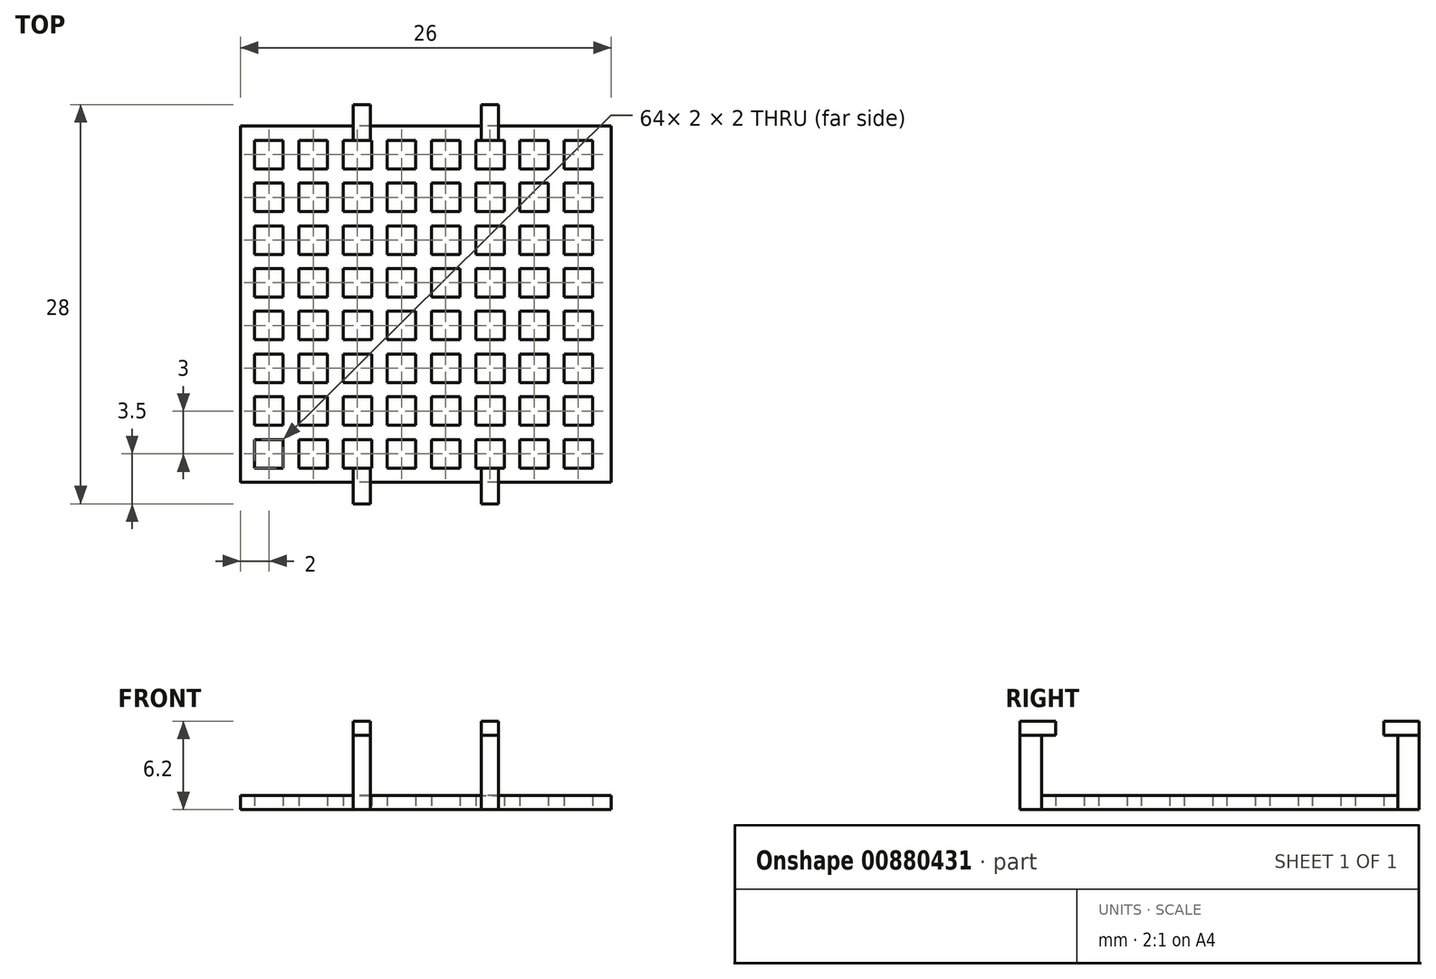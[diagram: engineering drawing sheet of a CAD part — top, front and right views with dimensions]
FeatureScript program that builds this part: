
annotation { "Feature Type Name" : "Feature", "Feature Type Description" : "" }
export const myFeature = defineFeature(function(context is Context, id is Id, definition is map)
    precondition{}
    {
        {
            var Q0;
            Q0=qCreatedBy(makeId("Top.planeOp"),FACE);
            var sketch = newSketch(context, id + "F0", { "sketchPlane" : qUnion([Q0])});
            skLineSegment(sketch, "E0.bottom", {"start": v(13, -12.5) * mm, "end": v(-13, -12.5) * mm});
            skLineSegment(sketch, "E0.top", {"start": v(13, 12.5) * mm, "end": v(-13, 12.5) * mm});
            skLineSegment(sketch, "E0.left", {"start": v(13, -12.5) * mm, "end": v(13, 12.5) * mm});
            skLineSegment(sketch, "E0.right", {"start": v(-13, -12.5) * mm, "end": v(-13, 12.5) * mm});
            skPoint(sketch, "E0.middle", {"position": v(0, 0) * mm});
            skLineSegment(sketch, "E1.bottom", {"start": v(-12, 11.5) * mm, "end": v(-10, 11.5) * mm});
            skLineSegment(sketch, "E1.top", {"start": v(-12, 9.5) * mm, "end": v(-10, 9.5) * mm});
            skLineSegment(sketch, "E1.left", {"start": v(-12, 11.5) * mm, "end": v(-12, 9.5) * mm});
            skLineSegment(sketch, "E1.right", {"start": v(-10, 11.5) * mm, "end": v(-10, 9.5) * mm});
            skLineSegment(sketch, "E2.0.1.0", {"start": v(-12, 8.5) * mm, "end": v(-10, 8.5) * mm});
            skLineSegment(sketch, "E2.0.1.1", {"start": v(-10, 8.5) * mm, "end": v(-10, 6.5) * mm});
            skLineSegment(sketch, "E2.0.1.2", {"start": v(-12, 8.5) * mm, "end": v(-12, 6.5) * mm});
            skLineSegment(sketch, "E2.0.1.3", {"start": v(-12, 6.5) * mm, "end": v(-10, 6.5) * mm});
            skLineSegment(sketch, "E2.0.2.0", {"start": v(-12, 5.5) * mm, "end": v(-10, 5.5) * mm});
            skLineSegment(sketch, "E2.0.2.1", {"start": v(-10, 5.5) * mm, "end": v(-10, 3.5) * mm});
            skLineSegment(sketch, "E2.0.2.2", {"start": v(-12, 5.5) * mm, "end": v(-12, 3.5) * mm});
            skLineSegment(sketch, "E2.0.2.3", {"start": v(-12, 3.5) * mm, "end": v(-10, 3.5) * mm});
            skLineSegment(sketch, "E2.0.3.0", {"start": v(-12, 2.5) * mm, "end": v(-10, 2.5) * mm});
            skLineSegment(sketch, "E2.0.3.1", {"start": v(-10, 2.5) * mm, "end": v(-10, 0.5) * mm});
            skLineSegment(sketch, "E2.0.3.2", {"start": v(-12, 2.5) * mm, "end": v(-12, 0.5) * mm});
            skLineSegment(sketch, "E2.0.3.3", {"start": v(-12, 0.5) * mm, "end": v(-10, 0.5) * mm});
            skLineSegment(sketch, "E2.0.4.0", {"start": v(-12, -0.5) * mm, "end": v(-10, -0.5) * mm});
            skLineSegment(sketch, "E2.0.4.1", {"start": v(-10, -0.5) * mm, "end": v(-10, -2.5) * mm});
            skLineSegment(sketch, "E2.0.4.2", {"start": v(-12, -0.5) * mm, "end": v(-12, -2.5) * mm});
            skLineSegment(sketch, "E2.0.4.3", {"start": v(-12, -2.5) * mm, "end": v(-10, -2.5) * mm});
            skLineSegment(sketch, "E2.0.5.0", {"start": v(-12, -3.5) * mm, "end": v(-10, -3.5) * mm});
            skLineSegment(sketch, "E2.0.5.1", {"start": v(-10, -3.5) * mm, "end": v(-10, -5.5) * mm});
            skLineSegment(sketch, "E2.0.5.2", {"start": v(-12, -3.5) * mm, "end": v(-12, -5.5) * mm});
            skLineSegment(sketch, "E2.0.5.3", {"start": v(-12, -5.5) * mm, "end": v(-10, -5.5) * mm});
            skLineSegment(sketch, "E2.0.6.0", {"start": v(-12, -6.5) * mm, "end": v(-10, -6.5) * mm});
            skLineSegment(sketch, "E2.0.6.1", {"start": v(-10, -6.5) * mm, "end": v(-10, -8.5) * mm});
            skLineSegment(sketch, "E2.0.6.2", {"start": v(-12, -6.5) * mm, "end": v(-12, -8.5) * mm});
            skLineSegment(sketch, "E2.0.6.3", {"start": v(-12, -8.5) * mm, "end": v(-10, -8.5) * mm});
            skLineSegment(sketch, "E2.0.7.0", {"start": v(-12, -9.5) * mm, "end": v(-10, -9.5) * mm});
            skLineSegment(sketch, "E2.0.7.1", {"start": v(-10, -9.5) * mm, "end": v(-10, -11.5) * mm});
            skLineSegment(sketch, "E2.0.7.2", {"start": v(-12, -9.5) * mm, "end": v(-12, -11.5) * mm});
            skLineSegment(sketch, "E2.0.7.3", {"start": v(-12, -11.5) * mm, "end": v(-10, -11.5) * mm});
            skLineSegment(sketch, "E2.1.0.0", {"start": v(-8.9, 11.5) * mm, "end": v(-6.9, 11.5) * mm});
            skLineSegment(sketch, "E2.1.0.1", {"start": v(-6.9, 11.5) * mm, "end": v(-6.9, 9.5) * mm});
            skLineSegment(sketch, "E2.1.0.2", {"start": v(-8.9, 11.5) * mm, "end": v(-8.9, 9.5) * mm});
            skLineSegment(sketch, "E2.1.0.3", {"start": v(-8.9, 9.5) * mm, "end": v(-6.9, 9.5) * mm});
            skLineSegment(sketch, "E2.1.1.0", {"start": v(-8.9, 8.5) * mm, "end": v(-6.9, 8.5) * mm});
            skLineSegment(sketch, "E2.1.1.1", {"start": v(-6.9, 8.5) * mm, "end": v(-6.9, 6.5) * mm});
            skLineSegment(sketch, "E2.1.1.2", {"start": v(-8.9, 8.5) * mm, "end": v(-8.9, 6.5) * mm});
            skLineSegment(sketch, "E2.1.1.3", {"start": v(-8.9, 6.5) * mm, "end": v(-6.9, 6.5) * mm});
            skLineSegment(sketch, "E2.1.2.0", {"start": v(-8.9, 5.5) * mm, "end": v(-6.9, 5.5) * mm});
            skLineSegment(sketch, "E2.1.2.1", {"start": v(-6.9, 5.5) * mm, "end": v(-6.9, 3.5) * mm});
            skLineSegment(sketch, "E2.1.2.2", {"start": v(-8.9, 5.5) * mm, "end": v(-8.9, 3.5) * mm});
            skLineSegment(sketch, "E2.1.2.3", {"start": v(-8.9, 3.5) * mm, "end": v(-6.9, 3.5) * mm});
            skLineSegment(sketch, "E2.1.3.0", {"start": v(-8.9, 2.5) * mm, "end": v(-6.9, 2.5) * mm});
            skLineSegment(sketch, "E2.1.3.1", {"start": v(-6.9, 2.5) * mm, "end": v(-6.9, 0.5) * mm});
            skLineSegment(sketch, "E2.1.3.2", {"start": v(-8.9, 2.5) * mm, "end": v(-8.9, 0.5) * mm});
            skLineSegment(sketch, "E2.1.3.3", {"start": v(-8.9, 0.5) * mm, "end": v(-6.9, 0.5) * mm});
            skLineSegment(sketch, "E2.1.4.0", {"start": v(-8.9, -0.5) * mm, "end": v(-6.9, -0.5) * mm});
            skLineSegment(sketch, "E2.1.4.1", {"start": v(-6.9, -0.5) * mm, "end": v(-6.9, -2.5) * mm});
            skLineSegment(sketch, "E2.1.4.2", {"start": v(-8.9, -0.5) * mm, "end": v(-8.9, -2.5) * mm});
            skLineSegment(sketch, "E2.1.4.3", {"start": v(-8.9, -2.5) * mm, "end": v(-6.9, -2.5) * mm});
            skLineSegment(sketch, "E2.1.5.0", {"start": v(-8.9, -3.5) * mm, "end": v(-6.9, -3.5) * mm});
            skLineSegment(sketch, "E2.1.5.1", {"start": v(-6.9, -3.5) * mm, "end": v(-6.9, -5.5) * mm});
            skLineSegment(sketch, "E2.1.5.2", {"start": v(-8.9, -3.5) * mm, "end": v(-8.9, -5.5) * mm});
            skLineSegment(sketch, "E2.1.5.3", {"start": v(-8.9, -5.5) * mm, "end": v(-6.9, -5.5) * mm});
            skLineSegment(sketch, "E2.1.6.0", {"start": v(-8.9, -6.5) * mm, "end": v(-6.9, -6.5) * mm});
            skLineSegment(sketch, "E2.1.6.1", {"start": v(-6.9, -6.5) * mm, "end": v(-6.9, -8.5) * mm});
            skLineSegment(sketch, "E2.1.6.2", {"start": v(-8.9, -6.5) * mm, "end": v(-8.9, -8.5) * mm});
            skLineSegment(sketch, "E2.1.6.3", {"start": v(-8.9, -8.5) * mm, "end": v(-6.9, -8.5) * mm});
            skLineSegment(sketch, "E2.1.7.0", {"start": v(-8.9, -9.5) * mm, "end": v(-6.9, -9.5) * mm});
            skLineSegment(sketch, "E2.1.7.1", {"start": v(-6.9, -9.5) * mm, "end": v(-6.9, -11.5) * mm});
            skLineSegment(sketch, "E2.1.7.2", {"start": v(-8.9, -9.5) * mm, "end": v(-8.9, -11.5) * mm});
            skLineSegment(sketch, "E2.1.7.3", {"start": v(-8.9, -11.5) * mm, "end": v(-6.9, -11.5) * mm});
            skLineSegment(sketch, "E2.2.0.0", {"start": v(-5.8, 11.5) * mm, "end": v(-3.8, 11.5) * mm});
            skLineSegment(sketch, "E2.2.0.1", {"start": v(-3.8, 11.5) * mm, "end": v(-3.8, 9.5) * mm});
            skLineSegment(sketch, "E2.2.0.2", {"start": v(-5.8, 11.5) * mm, "end": v(-5.8, 9.5) * mm});
            skLineSegment(sketch, "E2.2.0.3", {"start": v(-5.8, 9.5) * mm, "end": v(-3.8, 9.5) * mm});
            skLineSegment(sketch, "E2.2.1.0", {"start": v(-5.8, 8.5) * mm, "end": v(-3.8, 8.5) * mm});
            skLineSegment(sketch, "E2.2.1.1", {"start": v(-3.8, 8.5) * mm, "end": v(-3.8, 6.5) * mm});
            skLineSegment(sketch, "E2.2.1.2", {"start": v(-5.8, 8.5) * mm, "end": v(-5.8, 6.5) * mm});
            skLineSegment(sketch, "E2.2.1.3", {"start": v(-5.8, 6.5) * mm, "end": v(-3.8, 6.5) * mm});
            skLineSegment(sketch, "E2.2.2.0", {"start": v(-5.8, 5.5) * mm, "end": v(-3.8, 5.5) * mm});
            skLineSegment(sketch, "E2.2.2.1", {"start": v(-3.8, 5.5) * mm, "end": v(-3.8, 3.5) * mm});
            skLineSegment(sketch, "E2.2.2.2", {"start": v(-5.8, 5.5) * mm, "end": v(-5.8, 3.5) * mm});
            skLineSegment(sketch, "E2.2.2.3", {"start": v(-5.8, 3.5) * mm, "end": v(-3.8, 3.5) * mm});
            skLineSegment(sketch, "E2.2.3.0", {"start": v(-5.8, 2.5) * mm, "end": v(-3.8, 2.5) * mm});
            skLineSegment(sketch, "E2.2.3.1", {"start": v(-3.8, 2.5) * mm, "end": v(-3.8, 0.5) * mm});
            skLineSegment(sketch, "E2.2.3.2", {"start": v(-5.8, 2.5) * mm, "end": v(-5.8, 0.5) * mm});
            skLineSegment(sketch, "E2.2.3.3", {"start": v(-5.8, 0.5) * mm, "end": v(-3.8, 0.5) * mm});
            skLineSegment(sketch, "E2.2.4.0", {"start": v(-5.8, -0.5) * mm, "end": v(-3.8, -0.5) * mm});
            skLineSegment(sketch, "E2.2.4.1", {"start": v(-3.8, -0.5) * mm, "end": v(-3.8, -2.5) * mm});
            skLineSegment(sketch, "E2.2.4.2", {"start": v(-5.8, -0.5) * mm, "end": v(-5.8, -2.5) * mm});
            skLineSegment(sketch, "E2.2.4.3", {"start": v(-5.8, -2.5) * mm, "end": v(-3.8, -2.5) * mm});
            skLineSegment(sketch, "E2.2.5.0", {"start": v(-5.8, -3.5) * mm, "end": v(-3.8, -3.5) * mm});
            skLineSegment(sketch, "E2.2.5.1", {"start": v(-3.8, -3.5) * mm, "end": v(-3.8, -5.5) * mm});
            skLineSegment(sketch, "E2.2.5.2", {"start": v(-5.8, -3.5) * mm, "end": v(-5.8, -5.5) * mm});
            skLineSegment(sketch, "E2.2.5.3", {"start": v(-5.8, -5.5) * mm, "end": v(-3.8, -5.5) * mm});
            skLineSegment(sketch, "E2.2.6.0", {"start": v(-5.8, -6.5) * mm, "end": v(-3.8, -6.5) * mm});
            skLineSegment(sketch, "E2.2.6.1", {"start": v(-3.8, -6.5) * mm, "end": v(-3.8, -8.5) * mm});
            skLineSegment(sketch, "E2.2.6.2", {"start": v(-5.8, -6.5) * mm, "end": v(-5.8, -8.5) * mm});
            skLineSegment(sketch, "E2.2.6.3", {"start": v(-5.8, -8.5) * mm, "end": v(-3.8, -8.5) * mm});
            skLineSegment(sketch, "E2.2.7.0", {"start": v(-5.8, -9.5) * mm, "end": v(-3.8, -9.5) * mm});
            skLineSegment(sketch, "E2.2.7.1", {"start": v(-3.8, -9.5) * mm, "end": v(-3.8, -11.5) * mm});
            skLineSegment(sketch, "E2.2.7.2", {"start": v(-5.8, -9.5) * mm, "end": v(-5.8, -11.5) * mm});
            skLineSegment(sketch, "E2.2.7.3", {"start": v(-5.8, -11.5) * mm, "end": v(-3.8, -11.5) * mm});
            skLineSegment(sketch, "E2.3.0.0", {"start": v(-2.7, 11.5) * mm, "end": v(-0.7, 11.5) * mm});
            skLineSegment(sketch, "E2.3.0.1", {"start": v(-0.7, 11.5) * mm, "end": v(-0.7, 9.5) * mm});
            skLineSegment(sketch, "E2.3.0.2", {"start": v(-2.7, 11.5) * mm, "end": v(-2.7, 9.5) * mm});
            skLineSegment(sketch, "E2.3.0.3", {"start": v(-2.7, 9.5) * mm, "end": v(-0.7, 9.5) * mm});
            skLineSegment(sketch, "E2.3.1.0", {"start": v(-2.7, 8.5) * mm, "end": v(-0.7, 8.5) * mm});
            skLineSegment(sketch, "E2.3.1.1", {"start": v(-0.7, 8.5) * mm, "end": v(-0.7, 6.5) * mm});
            skLineSegment(sketch, "E2.3.1.2", {"start": v(-2.7, 8.5) * mm, "end": v(-2.7, 6.5) * mm});
            skLineSegment(sketch, "E2.3.1.3", {"start": v(-2.7, 6.5) * mm, "end": v(-0.7, 6.5) * mm});
            skLineSegment(sketch, "E2.3.2.0", {"start": v(-2.7, 5.5) * mm, "end": v(-0.7, 5.5) * mm});
            skLineSegment(sketch, "E2.3.2.1", {"start": v(-0.7, 5.5) * mm, "end": v(-0.7, 3.5) * mm});
            skLineSegment(sketch, "E2.3.2.2", {"start": v(-2.7, 5.5) * mm, "end": v(-2.7, 3.5) * mm});
            skLineSegment(sketch, "E2.3.2.3", {"start": v(-2.7, 3.5) * mm, "end": v(-0.7, 3.5) * mm});
            skLineSegment(sketch, "E2.3.3.0", {"start": v(-2.7, 2.5) * mm, "end": v(-0.7, 2.5) * mm});
            skLineSegment(sketch, "E2.3.3.1", {"start": v(-0.7, 2.5) * mm, "end": v(-0.7, 0.5) * mm});
            skLineSegment(sketch, "E2.3.3.2", {"start": v(-2.7, 2.5) * mm, "end": v(-2.7, 0.5) * mm});
            skLineSegment(sketch, "E2.3.3.3", {"start": v(-2.7, 0.5) * mm, "end": v(-0.7, 0.5) * mm});
            skLineSegment(sketch, "E2.3.4.0", {"start": v(-2.7, -0.5) * mm, "end": v(-0.7, -0.5) * mm});
            skLineSegment(sketch, "E2.3.4.1", {"start": v(-0.7, -0.5) * mm, "end": v(-0.7, -2.5) * mm});
            skLineSegment(sketch, "E2.3.4.2", {"start": v(-2.7, -0.5) * mm, "end": v(-2.7, -2.5) * mm});
            skLineSegment(sketch, "E2.3.4.3", {"start": v(-2.7, -2.5) * mm, "end": v(-0.7, -2.5) * mm});
            skLineSegment(sketch, "E2.3.5.0", {"start": v(-2.7, -3.5) * mm, "end": v(-0.7, -3.5) * mm});
            skLineSegment(sketch, "E2.3.5.1", {"start": v(-0.7, -3.5) * mm, "end": v(-0.7, -5.5) * mm});
            skLineSegment(sketch, "E2.3.5.2", {"start": v(-2.7, -3.5) * mm, "end": v(-2.7, -5.5) * mm});
            skLineSegment(sketch, "E2.3.5.3", {"start": v(-2.7, -5.5) * mm, "end": v(-0.7, -5.5) * mm});
            skLineSegment(sketch, "E2.3.6.0", {"start": v(-2.7, -6.5) * mm, "end": v(-0.7, -6.5) * mm});
            skLineSegment(sketch, "E2.3.6.1", {"start": v(-0.7, -6.5) * mm, "end": v(-0.7, -8.5) * mm});
            skLineSegment(sketch, "E2.3.6.2", {"start": v(-2.7, -6.5) * mm, "end": v(-2.7, -8.5) * mm});
            skLineSegment(sketch, "E2.3.6.3", {"start": v(-2.7, -8.5) * mm, "end": v(-0.7, -8.5) * mm});
            skLineSegment(sketch, "E2.3.7.0", {"start": v(-2.7, -9.5) * mm, "end": v(-0.7, -9.5) * mm});
            skLineSegment(sketch, "E2.3.7.1", {"start": v(-0.7, -9.5) * mm, "end": v(-0.7, -11.5) * mm});
            skLineSegment(sketch, "E2.3.7.2", {"start": v(-2.7, -9.5) * mm, "end": v(-2.7, -11.5) * mm});
            skLineSegment(sketch, "E2.3.7.3", {"start": v(-2.7, -11.5) * mm, "end": v(-0.7, -11.5) * mm});
            skLineSegment(sketch, "E2.4.0.0", {"start": v(0.4, 11.5) * mm, "end": v(2.4, 11.5) * mm});
            skLineSegment(sketch, "E2.4.0.1", {"start": v(2.4, 11.5) * mm, "end": v(2.4, 9.5) * mm});
            skLineSegment(sketch, "E2.4.0.2", {"start": v(0.4, 11.5) * mm, "end": v(0.4, 9.5) * mm});
            skLineSegment(sketch, "E2.4.0.3", {"start": v(0.4, 9.5) * mm, "end": v(2.4, 9.5) * mm});
            skLineSegment(sketch, "E2.4.1.0", {"start": v(0.4, 8.5) * mm, "end": v(2.4, 8.5) * mm});
            skLineSegment(sketch, "E2.4.1.1", {"start": v(2.4, 8.5) * mm, "end": v(2.4, 6.5) * mm});
            skLineSegment(sketch, "E2.4.1.2", {"start": v(0.4, 8.5) * mm, "end": v(0.4, 6.5) * mm});
            skLineSegment(sketch, "E2.4.1.3", {"start": v(0.4, 6.5) * mm, "end": v(2.4, 6.5) * mm});
            skLineSegment(sketch, "E2.4.2.0", {"start": v(0.4, 5.5) * mm, "end": v(2.4, 5.5) * mm});
            skLineSegment(sketch, "E2.4.2.1", {"start": v(2.4, 5.5) * mm, "end": v(2.4, 3.5) * mm});
            skLineSegment(sketch, "E2.4.2.2", {"start": v(0.4, 5.5) * mm, "end": v(0.4, 3.5) * mm});
            skLineSegment(sketch, "E2.4.2.3", {"start": v(0.4, 3.5) * mm, "end": v(2.4, 3.5) * mm});
            skLineSegment(sketch, "E2.4.3.0", {"start": v(0.4, 2.5) * mm, "end": v(2.4, 2.5) * mm});
            skLineSegment(sketch, "E2.4.3.1", {"start": v(2.4, 2.5) * mm, "end": v(2.4, 0.5) * mm});
            skLineSegment(sketch, "E2.4.3.2", {"start": v(0.4, 2.5) * mm, "end": v(0.4, 0.5) * mm});
            skLineSegment(sketch, "E2.4.3.3", {"start": v(0.4, 0.5) * mm, "end": v(2.4, 0.5) * mm});
            skLineSegment(sketch, "E2.4.4.0", {"start": v(0.4, -0.5) * mm, "end": v(2.4, -0.5) * mm});
            skLineSegment(sketch, "E2.4.4.1", {"start": v(2.4, -0.5) * mm, "end": v(2.4, -2.5) * mm});
            skLineSegment(sketch, "E2.4.4.2", {"start": v(0.4, -0.5) * mm, "end": v(0.4, -2.5) * mm});
            skLineSegment(sketch, "E2.4.4.3", {"start": v(0.4, -2.5) * mm, "end": v(2.4, -2.5) * mm});
            skLineSegment(sketch, "E2.4.5.0", {"start": v(0.4, -3.5) * mm, "end": v(2.4, -3.5) * mm});
            skLineSegment(sketch, "E2.4.5.1", {"start": v(2.4, -3.5) * mm, "end": v(2.4, -5.5) * mm});
            skLineSegment(sketch, "E2.4.5.2", {"start": v(0.4, -3.5) * mm, "end": v(0.4, -5.5) * mm});
            skLineSegment(sketch, "E2.4.5.3", {"start": v(0.4, -5.5) * mm, "end": v(2.4, -5.5) * mm});
            skLineSegment(sketch, "E2.4.6.0", {"start": v(0.4, -6.5) * mm, "end": v(2.4, -6.5) * mm});
            skLineSegment(sketch, "E2.4.6.1", {"start": v(2.4, -6.5) * mm, "end": v(2.4, -8.5) * mm});
            skLineSegment(sketch, "E2.4.6.2", {"start": v(0.4, -6.5) * mm, "end": v(0.4, -8.5) * mm});
            skLineSegment(sketch, "E2.4.6.3", {"start": v(0.4, -8.5) * mm, "end": v(2.4, -8.5) * mm});
            skLineSegment(sketch, "E2.4.7.0", {"start": v(0.4, -9.5) * mm, "end": v(2.4, -9.5) * mm});
            skLineSegment(sketch, "E2.4.7.1", {"start": v(2.4, -9.5) * mm, "end": v(2.4, -11.5) * mm});
            skLineSegment(sketch, "E2.4.7.2", {"start": v(0.4, -9.5) * mm, "end": v(0.4, -11.5) * mm});
            skLineSegment(sketch, "E2.4.7.3", {"start": v(0.4, -11.5) * mm, "end": v(2.4, -11.5) * mm});
            skLineSegment(sketch, "E2.5.0.0", {"start": v(3.5, 11.5) * mm, "end": v(5.5, 11.5) * mm});
            skLineSegment(sketch, "E2.5.0.1", {"start": v(5.5, 11.5) * mm, "end": v(5.5, 9.5) * mm});
            skLineSegment(sketch, "E2.5.0.2", {"start": v(3.5, 11.5) * mm, "end": v(3.5, 9.5) * mm});
            skLineSegment(sketch, "E2.5.0.3", {"start": v(3.5, 9.5) * mm, "end": v(5.5, 9.5) * mm});
            skLineSegment(sketch, "E2.5.1.0", {"start": v(3.5, 8.5) * mm, "end": v(5.5, 8.5) * mm});
            skLineSegment(sketch, "E2.5.1.1", {"start": v(5.5, 8.5) * mm, "end": v(5.5, 6.5) * mm});
            skLineSegment(sketch, "E2.5.1.2", {"start": v(3.5, 8.5) * mm, "end": v(3.5, 6.5) * mm});
            skLineSegment(sketch, "E2.5.1.3", {"start": v(3.5, 6.5) * mm, "end": v(5.5, 6.5) * mm});
            skLineSegment(sketch, "E2.5.2.0", {"start": v(3.5, 5.5) * mm, "end": v(5.5, 5.5) * mm});
            skLineSegment(sketch, "E2.5.2.1", {"start": v(5.5, 5.5) * mm, "end": v(5.5, 3.5) * mm});
            skLineSegment(sketch, "E2.5.2.2", {"start": v(3.5, 5.5) * mm, "end": v(3.5, 3.5) * mm});
            skLineSegment(sketch, "E2.5.2.3", {"start": v(3.5, 3.5) * mm, "end": v(5.5, 3.5) * mm});
            skLineSegment(sketch, "E2.5.3.0", {"start": v(3.5, 2.5) * mm, "end": v(5.5, 2.5) * mm});
            skLineSegment(sketch, "E2.5.3.1", {"start": v(5.5, 2.5) * mm, "end": v(5.5, 0.5) * mm});
            skLineSegment(sketch, "E2.5.3.2", {"start": v(3.5, 2.5) * mm, "end": v(3.5, 0.5) * mm});
            skLineSegment(sketch, "E2.5.3.3", {"start": v(3.5, 0.5) * mm, "end": v(5.5, 0.5) * mm});
            skLineSegment(sketch, "E2.5.4.0", {"start": v(3.5, -0.5) * mm, "end": v(5.5, -0.5) * mm});
            skLineSegment(sketch, "E2.5.4.1", {"start": v(5.5, -0.5) * mm, "end": v(5.5, -2.5) * mm});
            skLineSegment(sketch, "E2.5.4.2", {"start": v(3.5, -0.5) * mm, "end": v(3.5, -2.5) * mm});
            skLineSegment(sketch, "E2.5.4.3", {"start": v(3.5, -2.5) * mm, "end": v(5.5, -2.5) * mm});
            skLineSegment(sketch, "E2.5.5.0", {"start": v(3.5, -3.5) * mm, "end": v(5.5, -3.5) * mm});
            skLineSegment(sketch, "E2.5.5.1", {"start": v(5.5, -3.5) * mm, "end": v(5.5, -5.5) * mm});
            skLineSegment(sketch, "E2.5.5.2", {"start": v(3.5, -3.5) * mm, "end": v(3.5, -5.5) * mm});
            skLineSegment(sketch, "E2.5.5.3", {"start": v(3.5, -5.5) * mm, "end": v(5.5, -5.5) * mm});
            skLineSegment(sketch, "E2.5.6.0", {"start": v(3.5, -6.5) * mm, "end": v(5.5, -6.5) * mm});
            skLineSegment(sketch, "E2.5.6.1", {"start": v(5.5, -6.5) * mm, "end": v(5.5, -8.5) * mm});
            skLineSegment(sketch, "E2.5.6.2", {"start": v(3.5, -6.5) * mm, "end": v(3.5, -8.5) * mm});
            skLineSegment(sketch, "E2.5.6.3", {"start": v(3.5, -8.5) * mm, "end": v(5.5, -8.5) * mm});
            skLineSegment(sketch, "E2.5.7.0", {"start": v(3.5, -9.5) * mm, "end": v(5.5, -9.5) * mm});
            skLineSegment(sketch, "E2.5.7.1", {"start": v(5.5, -9.5) * mm, "end": v(5.5, -11.5) * mm});
            skLineSegment(sketch, "E2.5.7.2", {"start": v(3.5, -9.5) * mm, "end": v(3.5, -11.5) * mm});
            skLineSegment(sketch, "E2.5.7.3", {"start": v(3.5, -11.5) * mm, "end": v(5.5, -11.5) * mm});
            skLineSegment(sketch, "E2.6.0.0", {"start": v(6.6, 11.5) * mm, "end": v(8.6, 11.5) * mm});
            skLineSegment(sketch, "E2.6.0.1", {"start": v(8.6, 11.5) * mm, "end": v(8.6, 9.5) * mm});
            skLineSegment(sketch, "E2.6.0.2", {"start": v(6.6, 11.5) * mm, "end": v(6.6, 9.5) * mm});
            skLineSegment(sketch, "E2.6.0.3", {"start": v(6.6, 9.5) * mm, "end": v(8.6, 9.5) * mm});
            skLineSegment(sketch, "E2.6.1.0", {"start": v(6.6, 8.5) * mm, "end": v(8.6, 8.5) * mm});
            skLineSegment(sketch, "E2.6.1.1", {"start": v(8.6, 8.5) * mm, "end": v(8.6, 6.5) * mm});
            skLineSegment(sketch, "E2.6.1.2", {"start": v(6.6, 8.5) * mm, "end": v(6.6, 6.5) * mm});
            skLineSegment(sketch, "E2.6.1.3", {"start": v(6.6, 6.5) * mm, "end": v(8.6, 6.5) * mm});
            skLineSegment(sketch, "E2.6.2.0", {"start": v(6.6, 5.5) * mm, "end": v(8.6, 5.5) * mm});
            skLineSegment(sketch, "E2.6.2.1", {"start": v(8.6, 5.5) * mm, "end": v(8.6, 3.5) * mm});
            skLineSegment(sketch, "E2.6.2.2", {"start": v(6.6, 5.5) * mm, "end": v(6.6, 3.5) * mm});
            skLineSegment(sketch, "E2.6.2.3", {"start": v(6.6, 3.5) * mm, "end": v(8.6, 3.5) * mm});
            skLineSegment(sketch, "E2.6.3.0", {"start": v(6.6, 2.5) * mm, "end": v(8.6, 2.5) * mm});
            skLineSegment(sketch, "E2.6.3.1", {"start": v(8.6, 2.5) * mm, "end": v(8.6, 0.5) * mm});
            skLineSegment(sketch, "E2.6.3.2", {"start": v(6.6, 2.5) * mm, "end": v(6.6, 0.5) * mm});
            skLineSegment(sketch, "E2.6.3.3", {"start": v(6.6, 0.5) * mm, "end": v(8.6, 0.5) * mm});
            skLineSegment(sketch, "E2.6.4.0", {"start": v(6.6, -0.5) * mm, "end": v(8.6, -0.5) * mm});
            skLineSegment(sketch, "E2.6.4.1", {"start": v(8.6, -0.5) * mm, "end": v(8.6, -2.5) * mm});
            skLineSegment(sketch, "E2.6.4.2", {"start": v(6.6, -0.5) * mm, "end": v(6.6, -2.5) * mm});
            skLineSegment(sketch, "E2.6.4.3", {"start": v(6.6, -2.5) * mm, "end": v(8.6, -2.5) * mm});
            skLineSegment(sketch, "E2.6.5.0", {"start": v(6.6, -3.5) * mm, "end": v(8.6, -3.5) * mm});
            skLineSegment(sketch, "E2.6.5.1", {"start": v(8.6, -3.5) * mm, "end": v(8.6, -5.5) * mm});
            skLineSegment(sketch, "E2.6.5.2", {"start": v(6.6, -3.5) * mm, "end": v(6.6, -5.5) * mm});
            skLineSegment(sketch, "E2.6.5.3", {"start": v(6.6, -5.5) * mm, "end": v(8.6, -5.5) * mm});
            skLineSegment(sketch, "E2.6.6.0", {"start": v(6.6, -6.5) * mm, "end": v(8.6, -6.5) * mm});
            skLineSegment(sketch, "E2.6.6.1", {"start": v(8.6, -6.5) * mm, "end": v(8.6, -8.5) * mm});
            skLineSegment(sketch, "E2.6.6.2", {"start": v(6.6, -6.5) * mm, "end": v(6.6, -8.5) * mm});
            skLineSegment(sketch, "E2.6.6.3", {"start": v(6.6, -8.5) * mm, "end": v(8.6, -8.5) * mm});
            skLineSegment(sketch, "E2.6.7.0", {"start": v(6.6, -9.5) * mm, "end": v(8.6, -9.5) * mm});
            skLineSegment(sketch, "E2.6.7.1", {"start": v(8.6, -9.5) * mm, "end": v(8.6, -11.5) * mm});
            skLineSegment(sketch, "E2.6.7.2", {"start": v(6.6, -9.5) * mm, "end": v(6.6, -11.5) * mm});
            skLineSegment(sketch, "E2.6.7.3", {"start": v(6.6, -11.5) * mm, "end": v(8.6, -11.5) * mm});
            skLineSegment(sketch, "E2.7.0.0", {"start": v(9.7, 11.5) * mm, "end": v(11.7, 11.5) * mm});
            skLineSegment(sketch, "E2.7.0.1", {"start": v(11.7, 11.5) * mm, "end": v(11.7, 9.5) * mm});
            skLineSegment(sketch, "E2.7.0.2", {"start": v(9.7, 11.5) * mm, "end": v(9.7, 9.5) * mm});
            skLineSegment(sketch, "E2.7.0.3", {"start": v(9.7, 9.5) * mm, "end": v(11.7, 9.5) * mm});
            skLineSegment(sketch, "E2.7.1.0", {"start": v(9.7, 8.5) * mm, "end": v(11.7, 8.5) * mm});
            skLineSegment(sketch, "E2.7.1.1", {"start": v(11.7, 8.5) * mm, "end": v(11.7, 6.5) * mm});
            skLineSegment(sketch, "E2.7.1.2", {"start": v(9.7, 8.5) * mm, "end": v(9.7, 6.5) * mm});
            skLineSegment(sketch, "E2.7.1.3", {"start": v(9.7, 6.5) * mm, "end": v(11.7, 6.5) * mm});
            skLineSegment(sketch, "E2.7.2.0", {"start": v(9.7, 5.5) * mm, "end": v(11.7, 5.5) * mm});
            skLineSegment(sketch, "E2.7.2.1", {"start": v(11.7, 5.5) * mm, "end": v(11.7, 3.5) * mm});
            skLineSegment(sketch, "E2.7.2.2", {"start": v(9.7, 5.5) * mm, "end": v(9.7, 3.5) * mm});
            skLineSegment(sketch, "E2.7.2.3", {"start": v(9.7, 3.5) * mm, "end": v(11.7, 3.5) * mm});
            skLineSegment(sketch, "E2.7.3.0", {"start": v(9.7, 2.5) * mm, "end": v(11.7, 2.5) * mm});
            skLineSegment(sketch, "E2.7.3.1", {"start": v(11.7, 2.5) * mm, "end": v(11.7, 0.5) * mm});
            skLineSegment(sketch, "E2.7.3.2", {"start": v(9.7, 2.5) * mm, "end": v(9.7, 0.5) * mm});
            skLineSegment(sketch, "E2.7.3.3", {"start": v(9.7, 0.5) * mm, "end": v(11.7, 0.5) * mm});
            skLineSegment(sketch, "E2.7.4.0", {"start": v(9.7, -0.5) * mm, "end": v(11.7, -0.5) * mm});
            skLineSegment(sketch, "E2.7.4.1", {"start": v(11.7, -0.5) * mm, "end": v(11.7, -2.5) * mm});
            skLineSegment(sketch, "E2.7.4.2", {"start": v(9.7, -0.5) * mm, "end": v(9.7, -2.5) * mm});
            skLineSegment(sketch, "E2.7.4.3", {"start": v(9.7, -2.5) * mm, "end": v(11.7, -2.5) * mm});
            skLineSegment(sketch, "E2.7.5.0", {"start": v(9.7, -3.5) * mm, "end": v(11.7, -3.5) * mm});
            skLineSegment(sketch, "E2.7.5.1", {"start": v(11.7, -3.5) * mm, "end": v(11.7, -5.5) * mm});
            skLineSegment(sketch, "E2.7.5.2", {"start": v(9.7, -3.5) * mm, "end": v(9.7, -5.5) * mm});
            skLineSegment(sketch, "E2.7.5.3", {"start": v(9.7, -5.5) * mm, "end": v(11.7, -5.5) * mm});
            skLineSegment(sketch, "E2.7.6.0", {"start": v(9.7, -6.5) * mm, "end": v(11.7, -6.5) * mm});
            skLineSegment(sketch, "E2.7.6.1", {"start": v(11.7, -6.5) * mm, "end": v(11.7, -8.5) * mm});
            skLineSegment(sketch, "E2.7.6.2", {"start": v(9.7, -6.5) * mm, "end": v(9.7, -8.5) * mm});
            skLineSegment(sketch, "E2.7.6.3", {"start": v(9.7, -8.5) * mm, "end": v(11.7, -8.5) * mm});
            skLineSegment(sketch, "E2.7.7.0", {"start": v(9.7, -9.5) * mm, "end": v(11.7, -9.5) * mm});
            skLineSegment(sketch, "E2.7.7.1", {"start": v(11.7, -9.5) * mm, "end": v(11.7, -11.5) * mm});
            skLineSegment(sketch, "E2.7.7.2", {"start": v(9.7, -9.5) * mm, "end": v(9.7, -11.5) * mm});
            skLineSegment(sketch, "E2.7.7.3", {"start": v(9.7, -11.5) * mm, "end": v(11.7, -11.5) * mm});
            skLineSegment(sketch, "E2.direction1", {"start": v(-12, 9.5) * mm, "end": v(-8.9, 9.5) * mm, "construction": true});
            skLineSegment(sketch, "E2.direction2", {"start": v(-12, 9.5) * mm, "end": v(-12, 6.5) * mm, "construction": true});
            skLineSegment(sketch, "E3", {"start": v(4.5, -11.5) * mm, "end": v(4.5, -10.2) * mm, "construction": true});
            skLineSegment(sketch, "E4", {"start": v(4.5, -10.2) * mm, "end": v(4.5, -14.8) * mm, "construction": true});
            skLineSegment(sketch, "E5.bottom", {"start": v(4.5, -12.5) * mm, "end": v(5.1, -12.5) * mm});
            skLineSegment(sketch, "E5.top", {"start": v(4.5, -14) * mm, "end": v(5.1, -14) * mm});
            skLineSegment(sketch, "E5.left", {"start": v(4.5, -12.5) * mm, "end": v(4.5, -14) * mm});
            skLineSegment(sketch, "E5.right", {"start": v(5.1, -12.5) * mm, "end": v(5.1, -14) * mm});
            skLineSegment(sketch, "E6.MirrorCS", {"start": v(4.5, -14) * mm, "end": v(3.9, -14) * mm});
            skLineSegment(sketch, "E7.MirrorCS", {"start": v(4.5, -12.5) * mm, "end": v(3.9, -12.5) * mm});
            skLineSegment(sketch, "E8.MirrorCS", {"start": v(3.9, -12.5) * mm, "end": v(3.9, -14) * mm});
            skLineSegment(sketch, "E9.MirrorCS", {"start": v(-4.5, -12.5) * mm, "end": v(-4.5, -14) * mm});
            skLineSegment(sketch, "E10.MirrorCS", {"start": v(-5.1, -12.5) * mm, "end": v(-5.1, -14) * mm});
            skLineSegment(sketch, "E11.MirrorCS", {"start": v(-4.5, -12.5) * mm, "end": v(-5.1, -12.5) * mm});
            skLineSegment(sketch, "E12.MirrorCS", {"start": v(-4.5, -14) * mm, "end": v(-5.1, -14) * mm});
            skLineSegment(sketch, "E13.MirrorCS", {"start": v(-4.5, -12.5) * mm, "end": v(-3.9, -12.5) * mm});
            skLineSegment(sketch, "E14.MirrorCS", {"start": v(-3.9, -12.5) * mm, "end": v(-3.9, -14) * mm});
            skLineSegment(sketch, "E15.MirrorCS", {"start": v(-4.5, -14) * mm, "end": v(-3.9, -14) * mm});
            skLineSegment(sketch, "E16.MirrorCS", {"start": v(-4.5, 12.5) * mm, "end": v(-4.5, 14) * mm});
            skLineSegment(sketch, "E17.MirrorCS", {"start": v(4.5, 12.5) * mm, "end": v(4.5, 14) * mm});
            skLineSegment(sketch, "E18.MirrorCS", {"start": v(-4.5, 14) * mm, "end": v(-5.1, 14) * mm});
            skLineSegment(sketch, "E19.MirrorCS", {"start": v(5.1, 12.5) * mm, "end": v(5.1, 14) * mm});
            skLineSegment(sketch, "E20.MirrorCS", {"start": v(-4.5, 12.5) * mm, "end": v(-3.9, 12.5) * mm});
            skLineSegment(sketch, "E21.MirrorCS", {"start": v(-5.1, 12.5) * mm, "end": v(-5.1, 14) * mm});
            skLineSegment(sketch, "E22.MirrorCS", {"start": v(4.5, 14) * mm, "end": v(5.1, 14) * mm});
            skLineSegment(sketch, "E23.MirrorCS", {"start": v(-4.5, 12.5) * mm, "end": v(-5.1, 12.5) * mm});
            skLineSegment(sketch, "E24.MirrorCS", {"start": v(4.5, 12.5) * mm, "end": v(5.1, 12.5) * mm});
            skLineSegment(sketch, "E25.MirrorCS", {"start": v(4.5, 12.5) * mm, "end": v(3.9, 12.5) * mm});
            skLineSegment(sketch, "E26.MirrorCS", {"start": v(3.9, 12.5) * mm, "end": v(3.9, 14) * mm});
            skLineSegment(sketch, "E27.MirrorCS", {"start": v(-4.5, 14) * mm, "end": v(-3.9, 14) * mm});
            skLineSegment(sketch, "E28.MirrorCS", {"start": v(4.5, 14) * mm, "end": v(3.9, 14) * mm});
            skLineSegment(sketch, "E29.MirrorCS", {"start": v(-3.9, 12.5) * mm, "end": v(-3.9, 14) * mm});
            skSolve(sketch);
        }
        {
            var Q0;
            Q0=makeQuery(id+"F0.imprint","IMPRINT",FACE,{"disambiguationData":[TD([[makeQuery(id+"F0.imprint","IMPRINT",EDGE,{"derivedFrom":sQuery(id+"F0.wireOp",EDGE,"E0.bottom")}),-1.0]])]});
            extrude(context, id + "F1", {"entities" : qUnion([Q0]), "depth" : 1 * mm, "offsetDistance" : 25 * mm});
        }
        {
            var Q0;
            {var subQ5=sQuery(id+"F0.wireOp",EDGE,"E5.top");Q0=makeQuery(id+"F0.imprint","IMPRINT",FACE,{"disambiguationData":[TD([[makeQuery(id+"F0.imprint","IMPRINT",EDGE,{"derivedFrom":subQ5}),1.0]])]});}
            var Q1;
            {var subQ5=sQuery(id+"F0.wireOp",EDGE,"E6.MirrorCS");Q1=makeQuery(id+"F0.imprint","IMPRINT",FACE,{"disambiguationData":[TD([[makeQuery(id+"F0.imprint","IMPRINT",EDGE,{"derivedFrom":subQ5}),-1.0]])]});}
            var Q2;
            {var subQ5=sQuery(id+"F0.wireOp",EDGE,"E15.MirrorCS");Q2=makeQuery(id+"F0.imprint","IMPRINT",FACE,{"disambiguationData":[TD([[makeQuery(id+"F0.imprint","IMPRINT",EDGE,{"derivedFrom":subQ5}),1.0]])]});}
            var Q3;
            {var subQ5=sQuery(id+"F0.wireOp",EDGE,"E12.MirrorCS");Q3=makeQuery(id+"F0.imprint","IMPRINT",FACE,{"disambiguationData":[TD([[makeQuery(id+"F0.imprint","IMPRINT",EDGE,{"derivedFrom":subQ5}),-1.0]])]});}
            var Q4;
            {var subQ5=sQuery(id+"F0.wireOp",EDGE,"E22.MirrorCS");Q4=makeQuery(id+"F0.imprint","IMPRINT",FACE,{"disambiguationData":[TD([[makeQuery(id+"F0.imprint","IMPRINT",EDGE,{"derivedFrom":subQ5}),-1.0]])]});}
            var Q5;
            {var subQ5=sQuery(id+"F0.wireOp",EDGE,"E28.MirrorCS");Q5=makeQuery(id+"F0.imprint","IMPRINT",FACE,{"disambiguationData":[TD([[makeQuery(id+"F0.imprint","IMPRINT",EDGE,{"derivedFrom":subQ5}),1.0]])]});}
            var Q6;
            {var subQ5=sQuery(id+"F0.wireOp",EDGE,"E27.MirrorCS");Q6=makeQuery(id+"F0.imprint","IMPRINT",FACE,{"disambiguationData":[TD([[makeQuery(id+"F0.imprint","IMPRINT",EDGE,{"derivedFrom":subQ5}),-1.0]])]});}
            var Q7;
            {var subQ5=sQuery(id+"F0.wireOp",EDGE,"E18.MirrorCS");Q7=makeQuery(id+"F0.imprint","IMPRINT",FACE,{"disambiguationData":[TD([[makeQuery(id+"F0.imprint","IMPRINT",EDGE,{"derivedFrom":subQ5}),1.0]])]});}
            extrude(context, id + "F2", {"entities" : qUnion([Q0, Q1, Q2, Q3, Q4, Q5, Q6, Q7]), "depth" : 5.2 * mm, "offsetDistance" : 25 * mm});
        }
        {
            var Q0;
            Q0=makeQuery(id+"F2.opExtrude","CAP_FACE",FACE,{"disambiguationData":[OSD([sQuery(id+"F0.wireOp",EDGE,"E0.bottom"),sQuery(id+"F0.wireOp",EDGE,"E5.top"),sQuery(id+"F0.wireOp",EDGE,"E5.right"),sQuery(id+"F0.wireOp",EDGE,"E6.MirrorCS"),sQuery(id+"F0.wireOp",EDGE,"E8.MirrorCS")])],"isStart":false});
            var sketch = newSketch(context, id + "F3", { "sketchPlane" : qUnion([Q0])});
            skLineSegment(sketch, "E30.bottom", {"start": v(5.1, -14) * mm, "end": v(3.9, -14) * mm});
            skLineSegment(sketch, "E30.top", {"start": v(5.1, -11.5) * mm, "end": v(3.9, -11.5) * mm});
            skLineSegment(sketch, "E30.left", {"start": v(5.1, -14) * mm, "end": v(5.1, -11.5) * mm});
            skLineSegment(sketch, "E30.right", {"start": v(3.9, -14) * mm, "end": v(3.9, -11.5) * mm});
            skLineSegment(sketch, "E31.MirrorCS", {"start": v(-5.1, -11.5) * mm, "end": v(-3.9, -11.5) * mm});
            skLineSegment(sketch, "E32.MirrorCS", {"start": v(-5.1, -14) * mm, "end": v(-3.9, -14) * mm});
            skLineSegment(sketch, "E33.MirrorCS", {"start": v(-5.1, -14) * mm, "end": v(-5.1, -11.5) * mm});
            skLineSegment(sketch, "E34.MirrorCS", {"start": v(-3.9, -14) * mm, "end": v(-3.9, -11.5) * mm});
            skLineSegment(sketch, "E35.MirrorCS", {"start": v(5.1, 14) * mm, "end": v(3.9, 14) * mm});
            skLineSegment(sketch, "E36.MirrorCS", {"start": v(-5.1, 14) * mm, "end": v(-3.9, 14) * mm});
            skLineSegment(sketch, "E37.MirrorCS", {"start": v(3.9, 14) * mm, "end": v(3.9, 11.5) * mm});
            skLineSegment(sketch, "E38.MirrorCS", {"start": v(-5.1, 14) * mm, "end": v(-5.1, 11.5) * mm});
            skLineSegment(sketch, "E39.MirrorCS", {"start": v(-3.9, 14) * mm, "end": v(-3.9, 11.5) * mm});
            skLineSegment(sketch, "E40.MirrorCS", {"start": v(5.1, 11.5) * mm, "end": v(3.9, 11.5) * mm});
            skLineSegment(sketch, "E41.MirrorCS", {"start": v(5.1, 14) * mm, "end": v(5.1, 11.5) * mm});
            skLineSegment(sketch, "E42.MirrorCS", {"start": v(-5.1, 11.5) * mm, "end": v(-3.9, 11.5) * mm});
            skSolve(sketch);
        }
        {
            var Q0;
            Q0=makeQuery(id+"F3.imprint","IMPRINT",FACE,{"disambiguationData":[TD([[makeQuery(id+"F3.imprint","IMPRINT",EDGE,{"derivedFrom":sQuery(id+"F3.wireOp",EDGE,"E35.MirrorCS")}),1.0]])]});
            var Q1;
            Q1=makeQuery(id+"F3.imprint","IMPRINT",FACE,{"disambiguationData":[TD([[makeQuery(id+"F3.imprint","IMPRINT",EDGE,{"derivedFrom":sQuery(id+"F3.wireOp",EDGE,"E36.MirrorCS")}),-1.0]])]});
            var Q2;
            {var subQ6=sQuery(id+"F3.wireOp",EDGE,"E30.top");Q2=makeQuery(id+"F3.imprint","IMPRINT",FACE,{"disambiguationData":[TD([[makeQuery(id+"F3.imprint","IMPRINT",EDGE,{"derivedFrom":subQ6}),1.0]])]});}
            var Q3;
            Q3=makeQuery(id+"F3.imprint","IMPRINT",FACE,{"disambiguationData":[TD([[makeQuery(id+"F3.imprint","IMPRINT",EDGE,{"derivedFrom":sQuery(id+"F3.wireOp",EDGE,"E31.MirrorCS")}),-1.0]])]});
            var Q4;
            {var subQ3=sQuery(id+"F0.wireOp",EDGE,"E8.MirrorCS");var subQ4=makeQuery(id+"F2.opExtrude","CAP_EDGE",EDGE,{"disambiguationData":[OSD([subQ3])],"isStart":false});Q4=makeQuery(id+"F3.imprint","IMPRINT",FACE,{"disambiguationData":[TD([[makeQuery(id+"F3.imprint","IMPRINT",EDGE,{"derivedFrom":subQ4}),1.0]])]});}
            var Q5;
            {var subQ0=sQuery(id+"F3.wireOp",EDGE,"E30.bottom");Q5=makeQuery(id+"F3.imprint","IMPRINT",FACE,{"disambiguationData":[TD([[makeQuery(id+"F3.imprint","IMPRINT",EDGE,{"derivedFrom":subQ0}),1.0]])]});}
            extrude(context, id + "F4", {"entities" : qUnion([Q0, Q1, Q2, Q3, Q4, Q5]), "depth" : 1 * mm, "offsetDistance" : 25 * mm});
        }
    });
